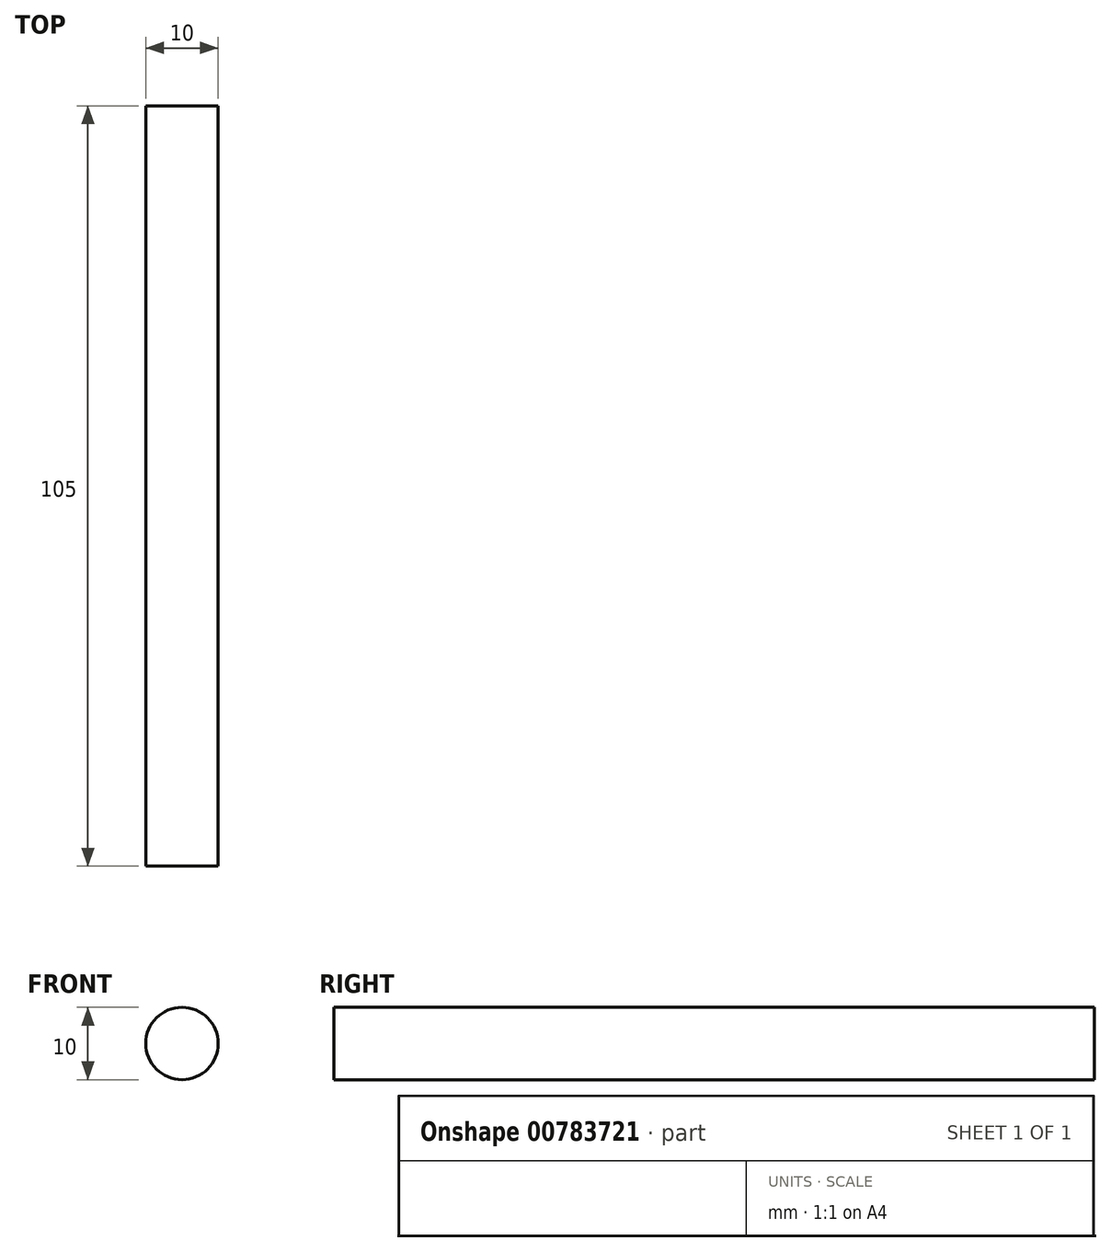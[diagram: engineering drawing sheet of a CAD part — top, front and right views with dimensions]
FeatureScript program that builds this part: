
annotation { "Feature Type Name" : "Feature", "Feature Type Description" : "" }
export const myFeature = defineFeature(function(context is Context, id is Id, definition is map)
    precondition{}
    {
        {
            var Q0;
            Q0=qCreatedBy(makeId("Front.planeOp"),FACE);
            var sketch = newSketch(context, id + "F0", { "sketchPlane" : qUnion([Q0])});
            skCircle(sketch, "E0", {"center": v(0, 0) * mm, "radius": 5 * mm});
            skSolve(sketch);
        }
        {
            var Q0;
            Q0=makeQuery(id+"F0.imprint","IMPRINT",FACE,{"disambiguationData":[TD([[makeQuery(id+"F0.imprint","IMPRINT",EDGE,{"derivedFrom":sQuery(id+"F0.wireOp",EDGE,"E0")}),1.0]])]});
            var Q1;
            Q1=sQuery(id+"F0.wireOp",EDGE,"E0");
            extrude(context, id + "F1", {"entities" : qUnion([Q0]), "surfaceEntities" : qUnion([Q1]), "depth" : 105 * mm, "offsetDistance" : 25 * mm});
        }
    });
